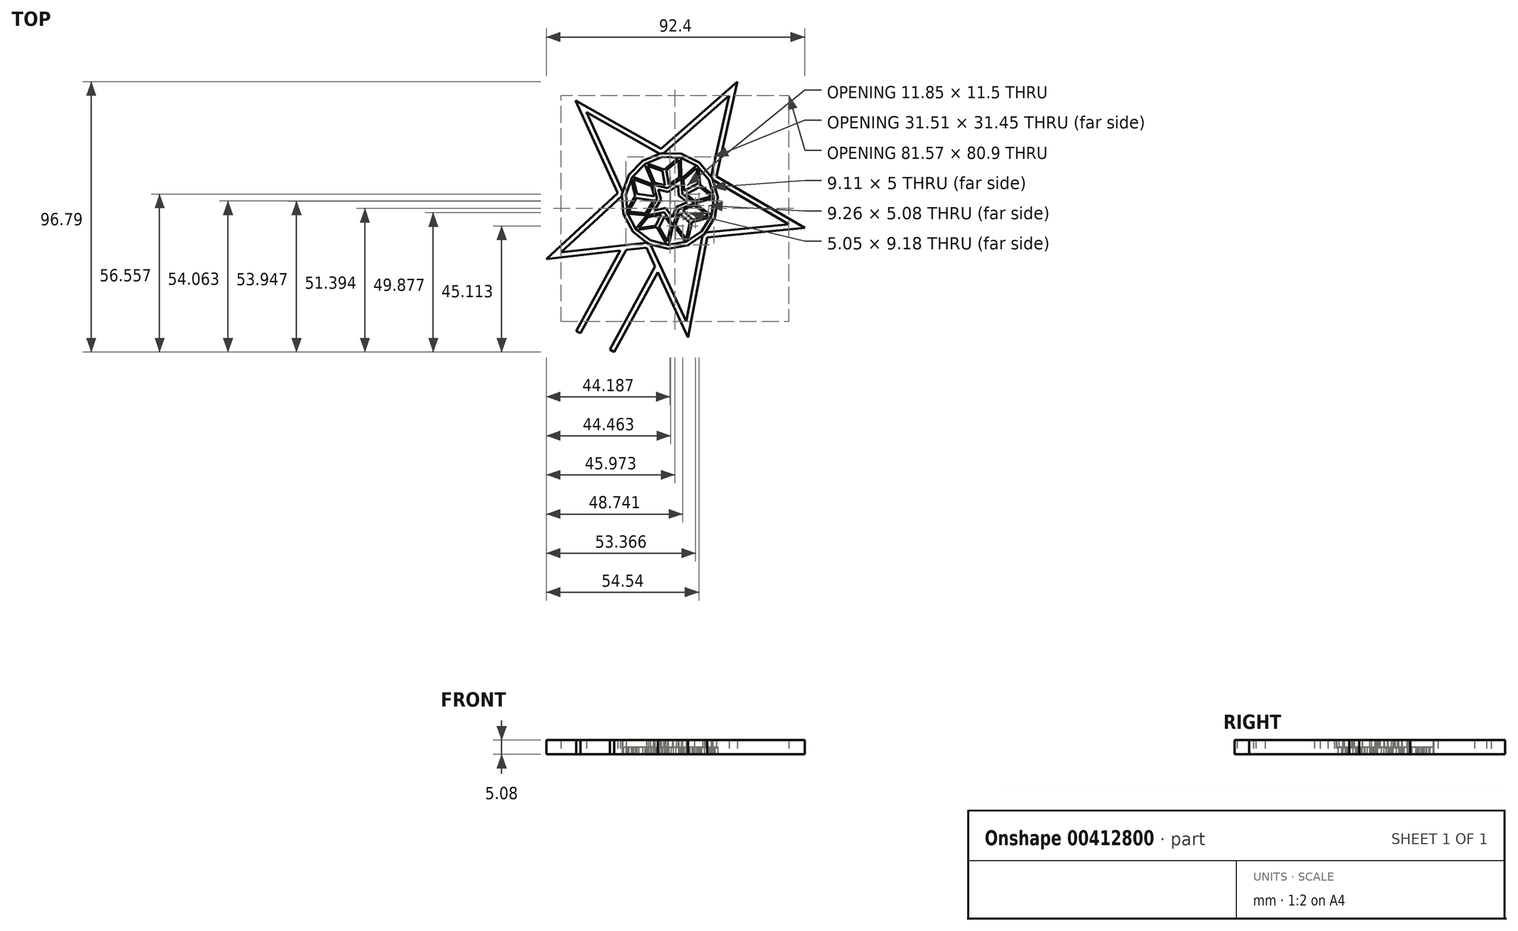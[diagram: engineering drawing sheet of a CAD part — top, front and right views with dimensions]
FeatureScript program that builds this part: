
annotation { "Feature Type Name" : "Feature", "Feature Type Description" : "" }
export const myFeature = defineFeature(function(context is Context, id is Id, definition is map)
    precondition{}
    {
        {
            var Q0;
            Q0=qCreatedBy(makeId("Top.planeOp"),FACE);
            var sketch = newSketch(context, id + "F0", { "sketchPlane" : qUnion([Q0])});
            skLineSegment(sketch, "E0", {"start": v(-1.96, 11.1) * mm, "end": v(-0.8, 4.49) * mm});
            skLineSegment(sketch, "E1", {"start": v(7.94, -7.66) * mm, "end": v(3.28, -3.16) * mm});
            skLineSegment(sketch, "E2", {"start": v(10.8, 5.75) * mm, "end": v(4.51, 2.4) * mm});
            skLineSegment(sketch, "E3", {"start": v(-12.4, 1.73) * mm, "end": v(-4.51, 0.63) * mm});
            skLineSegment(sketch, "E4", {"start": v(-4.65, -9.55) * mm, "end": v(-2, -4.1) * mm});
            skPoint(sketch, "E5.cCircle.perimeterSnap0", {"position": v(15.6, 4.49) * mm});
            skPoint(sketch, "E5.0.startSnap0", {"position": v(15.6, 4.49) * mm});
            skLineSegment(sketch, "E6", {"start": v(-8.26, 13.38) * mm, "end": v(-1.96, 11.1) * mm});
            skLineSegment(sketch, "E7", {"start": v(-1.96, 11.1) * mm, "end": v(3.16, 15.4) * mm});
            skLineSegment(sketch, "E8", {"start": v(10.8, 5.75) * mm, "end": v(10.32, 11.82) * mm});
            skLineSegment(sketch, "E9", {"start": v(10.8, 5.75) * mm, "end": v(15.57, 1.96) * mm});
            skLineSegment(sketch, "E10", {"start": v(6.46, -14.34) * mm, "end": v(7.94, -7.66) * mm});
            skLineSegment(sketch, "E11", {"start": v(7.94, -7.66) * mm, "end": v(14.57, -5.94) * mm});
            skLineSegment(sketch, "E12", {"start": v(-4.65, -9.55) * mm, "end": v(-1.08, -15.7) * mm});
            skLineSegment(sketch, "E13", {"start": v(-11.7, -10.54) * mm, "end": v(-4.65, -9.55) * mm});
            skLineSegment(sketch, "E14", {"start": v(-15.3, -3.42) * mm, "end": v(-12.4, 1.73) * mm});
            skLineSegment(sketch, "E15", {"start": v(-13.77, 7.5) * mm, "end": v(-12.4, 1.73) * mm});
            skLineSegment(sketch, "E16", {"start": v(-0.8, 4.49) * mm, "end": v(4.12, 7.8) * mm});
            skLineSegment(sketch, "E17", {"start": v(4.51, 2.4) * mm, "end": v(8.76, -0.93) * mm});
            skLineSegment(sketch, "E18", {"start": v(3.28, -3.16) * mm, "end": v(8.76, -0.93) * mm});
            skLineSegment(sketch, "E19", {"start": v(3.28, -3.16) * mm, "end": v(1.26, -8.69) * mm});
            skLineSegment(sketch, "E20", {"start": v(1.26, -8.69) * mm, "end": v(-2, -4.1) * mm});
            skLineSegment(sketch, "E21", {"start": v(-8.21, -5.33) * mm, "end": v(-2, -4.1) * mm});
            skLineSegment(sketch, "E22", {"start": v(-8.21, -5.33) * mm, "end": v(-4.51, 0.63) * mm});
            skLineSegment(sketch, "E23", {"start": v(-5.98, 5.76) * mm, "end": v(-4.51, 0.63) * mm});
            skLineSegment(sketch, "E24", {"start": v(-5.98, 5.76) * mm, "end": v(-0.8, 4.49) * mm});
            skLineSegment(sketch, "E25", {"start": v(-2.2, 16.96) * mm, "end": v(21.23, 37.66) * mm});
            skLineSegment(sketch, "E26", {"start": v(14.83, 8.59) * mm, "end": v(21.23, 37.66) * mm});
            skLineSegment(sketch, "E27", {"start": v(15.45, 7.34) * mm, "end": v(42.63, -8.47) * mm});
            skLineSegment(sketch, "E28", {"start": v(42.63, -8.47) * mm, "end": v(12.75, -11.45) * mm});
            skLineSegment(sketch, "E29", {"start": v(5.85, -43.24) * mm, "end": v(11.78, -12.4) * mm});
            skLineSegment(sketch, "E30", {"start": v(-6.93, -15.67) * mm, "end": v(5.85, -43.24) * mm});
            skLineSegment(sketch, "E31", {"start": v(-38.94, -18.5) * mm, "end": v(-8.17, -15.03) * mm});
            skLineSegment(sketch, "E32", {"start": v(-17.04, 1.75) * mm, "end": v(-38.94, -18.5) * mm});
            skLineSegment(sketch, "E33", {"start": v(-16.82, 3.13) * mm, "end": v(-29.8, 31.65) * mm});
            skLineSegment(sketch, "E34", {"start": v(-29.8, 31.65) * mm, "end": v(-3.6, 16.75) * mm});
            skPoint(sketch, "E35.orphan", {"position": v(-1.45, 8.17) * mm});
            skLineSegment(sketch, "E36", {"start": v(4.12, 7.8) * mm, "end": v(4.51, 2.4) * mm});
            skLineSegment(sketch, "E37", {"start": v(-13.33, 8.5) * mm, "end": v(-5.98, 5.76) * mm});
            skLineSegment(sketch, "E38", {"start": v(4.12, 7.8) * mm, "end": v(4.02, 15.29) * mm});
            skLineSegment(sketch, "E39", {"start": v(-8.99, 13.02) * mm, "end": v(-5.98, 5.76) * mm});
            skLineSegment(sketch, "E40", {"start": v(4.12, 7.8) * mm, "end": v(9.6, 12.56) * mm});
            skLineSegment(sketch, "E41", {"start": v(-8.21, -5.33) * mm, "end": v(-15.08, -4.67) * mm});
            skLineSegment(sketch, "E42", {"start": v(-8.21, -5.33) * mm, "end": v(-12.2, -10.07) * mm});
            skLineSegment(sketch, "E43", {"start": v(-0.39, -15.81) * mm, "end": v(1.26, -8.69) * mm});
            skLineSegment(sketch, "E44", {"start": v(5.74, -14.73) * mm, "end": v(1.26, -8.69) * mm});
            skLineSegment(sketch, "E45", {"start": v(8.76, -0.93) * mm, "end": v(15.79, 0.96) * mm});
            skLineSegment(sketch, "E46.0", {"start": v(-18.6, 2.73) * mm, "end": v(-44.13, -20.87) * mm});
            skLineSegment(sketch, "E46.1", {"start": v(-44.13, -20.87) * mm, "end": v(-8.34, -16.84) * mm});
            skLineSegment(sketch, "E46.2", {"start": v(-18.6, 2.73) * mm, "end": v(-33.7, 35.9) * mm});
            skLineSegment(sketch, "E46.3", {"start": v(-8.34, -16.84) * mm, "end": v(6.56, -48.99) * mm});
            skLineSegment(sketch, "E46.4", {"start": v(6.56, -48.99) * mm, "end": v(13.45, -13.16) * mm});
            skLineSegment(sketch, "E46.5", {"start": v(48.27, -9.7) * mm, "end": v(13.45, -13.16) * mm});
            skLineSegment(sketch, "E46.6", {"start": v(-33.7, 35.9) * mm, "end": v(-3.12, 18.52) * mm});
            skLineSegment(sketch, "E46.7", {"start": v(-3.12, 18.52) * mm, "end": v(24.14, 42.6) * mm});
            skLineSegment(sketch, "E46.8", {"start": v(16.67, 8.69) * mm, "end": v(24.14, 42.6) * mm});
            skLineSegment(sketch, "E46.9", {"start": v(16.67, 8.69) * mm, "end": v(48.27, -9.7) * mm});
            skLineSegment(sketch, "E47", {"start": v(8.76, -0.93) * mm, "end": v(14.93, -5.2) * mm});
            skLineSegment(sketch, "E48.0", {"start": v(-0.55, 3.12) * mm, "end": v(3.01, 5.52) * mm});
            skLineSegment(sketch, "E48.1", {"start": v(-4.15, 4) * mm, "end": v(-0.55, 3.12) * mm});
            skLineSegment(sketch, "E48.2", {"start": v(3.01, 5.52) * mm, "end": v(3.29, 1.75) * mm});
            skLineSegment(sketch, "E48.3", {"start": v(-4.15, 4) * mm, "end": v(-3.14, 0.44) * mm});
            skLineSegment(sketch, "E48.4", {"start": v(-5.6, -3.51) * mm, "end": v(-3.14, 0.44) * mm});
            skLineSegment(sketch, "E48.5", {"start": v(-5.6, -3.51) * mm, "end": v(-1.43, -2.7) * mm});
            skLineSegment(sketch, "E48.6", {"start": v(3.29, 1.75) * mm, "end": v(6.26, -0.58) * mm});
            skLineSegment(sketch, "E48.7", {"start": v(2.28, -2.2) * mm, "end": v(6.26, -0.58) * mm});
            skLineSegment(sketch, "E48.8", {"start": v(2.28, -2.2) * mm, "end": v(0.9, -5.98) * mm});
            skLineSegment(sketch, "E48.9", {"start": v(0.9, -5.98) * mm, "end": v(-1.43, -2.7) * mm});
            skLineSegment(sketch, "E49.0", {"start": v(-17.09, 2.4) * mm, "end": v(-14.64, 9.13) * mm});
            skLineSegment(sketch, "E49.1", {"start": v(-16.58, -4.77) * mm, "end": v(-17.09, 2.4) * mm});
            skLineSegment(sketch, "E49.2", {"start": v(-13.2, -11.1) * mm, "end": v(-16.58, -4.77) * mm});
            skLineSegment(sketch, "E49.3", {"start": v(-7.55, -15.51) * mm, "end": v(-13.2, -11.1) * mm});
            skLineSegment(sketch, "E49.4", {"start": v(10.61, 13.6) * mm, "end": v(15.23, 8.1) * mm});
            skLineSegment(sketch, "E49.5", {"start": v(4.16, 16.74) * mm, "end": v(10.61, 13.6) * mm});
            skLineSegment(sketch, "E49.6", {"start": v(-3, 16.99) * mm, "end": v(4.16, 16.74) * mm});
            skLineSegment(sketch, "E49.7", {"start": v(-9.66, 14.3) * mm, "end": v(-3, 16.99) * mm});
            skLineSegment(sketch, "E49.8", {"start": v(15.23, 8.1) * mm, "end": v(17.2, 1.21) * mm});
            skLineSegment(sketch, "E49.9", {"start": v(17.2, 1.21) * mm, "end": v(16.22, -5.9) * mm});
            skLineSegment(sketch, "E49.10", {"start": v(16.22, -5.9) * mm, "end": v(12.42, -11.98) * mm});
            skLineSegment(sketch, "E49.11", {"start": v(12.42, -11.98) * mm, "end": v(6.47, -16) * mm});
            skLineSegment(sketch, "E49.12", {"start": v(-14.64, 9.13) * mm, "end": v(-9.66, 14.3) * mm});
            skLineSegment(sketch, "E49.13", {"start": v(6.47, -16) * mm, "end": v(-0.6, -17.24) * mm});
            skLineSegment(sketch, "E49.14", {"start": v(-0.6, -17.24) * mm, "end": v(-7.55, -15.51) * mm});
            skLineSegment(sketch, "E50.0", {"start": v(-12, 0.93) * mm, "end": v(-5.74, 0.06) * mm});
            skLineSegment(sketch, "E50.1", {"start": v(-14.76, -3.96) * mm, "end": v(-12, 0.93) * mm});
            skLineSegment(sketch, "E50.2", {"start": v(-8.6, -4.55) * mm, "end": v(-14.76, -3.96) * mm});
            skLineSegment(sketch, "E50.3", {"start": v(-8.6, -4.55) * mm, "end": v(-5.74, 0.06) * mm});
            skLineSegment(sketch, "E51.0", {"start": v(-13.05, 7.62) * mm, "end": v(-6.58, 5.2) * mm});
            skLineSegment(sketch, "E51.1", {"start": v(-13.05, 7.62) * mm, "end": v(-11.8, 2.4) * mm});
            skLineSegment(sketch, "E51.2", {"start": v(-11.8, 2.4) * mm, "end": v(-5.53, 1.52) * mm});
            skLineSegment(sketch, "E51.3", {"start": v(-6.58, 5.2) * mm, "end": v(-5.53, 1.52) * mm});
            skLineSegment(sketch, "E52.0", {"start": v(-7.97, 12.5) * mm, "end": v(-2.62, 10.55) * mm});
            skLineSegment(sketch, "E52.1", {"start": v(-7.97, 12.5) * mm, "end": v(-5.44, 6.39) * mm});
            skLineSegment(sketch, "E52.2", {"start": v(-5.44, 6.39) * mm, "end": v(-1.72, 5.47) * mm});
            skLineSegment(sketch, "E52.3", {"start": v(-2.62, 10.55) * mm, "end": v(-1.72, 5.47) * mm});
            skLineSegment(sketch, "E53.0", {"start": v(-1.17, 10.8) * mm, "end": v(3.3, 14.55) * mm});
            skLineSegment(sketch, "E53.1", {"start": v(-1.17, 10.8) * mm, "end": v(-0.27, 5.73) * mm});
            skLineSegment(sketch, "E53.2", {"start": v(-0.27, 5.73) * mm, "end": v(3.38, 8.18) * mm});
            skLineSegment(sketch, "E53.3", {"start": v(3.38, 8.18) * mm, "end": v(3.3, 14.55) * mm});
            skLineSegment(sketch, "E54.0", {"start": v(4.88, 7.48) * mm, "end": v(9.6, 11.58) * mm});
            skLineSegment(sketch, "E54.1", {"start": v(4.88, 7.48) * mm, "end": v(5.16, 3.58) * mm});
            skLineSegment(sketch, "E54.2", {"start": v(10.03, 6.18) * mm, "end": v(5.16, 3.58) * mm});
            skLineSegment(sketch, "E54.3", {"start": v(10.03, 6.18) * mm, "end": v(9.6, 11.58) * mm});
            skLineSegment(sketch, "E55.0", {"start": v(10.72, 4.88) * mm, "end": v(14.96, 1.5) * mm});
            skLineSegment(sketch, "E55.1", {"start": v(10.72, 4.88) * mm, "end": v(5.86, 2.28) * mm});
            skLineSegment(sketch, "E55.2", {"start": v(5.86, 2.28) * mm, "end": v(8.93, -0.12) * mm});
            skLineSegment(sketch, "E55.3", {"start": v(8.93, -0.12) * mm, "end": v(14.96, 1.5) * mm});
            skLineSegment(sketch, "E56.0", {"start": v(4.6, -3.42) * mm, "end": v(8.67, -1.76) * mm});
            skLineSegment(sketch, "E56.1", {"start": v(8.16, -6.84) * mm, "end": v(4.6, -3.42) * mm});
            skLineSegment(sketch, "E56.2", {"start": v(8.16, -6.84) * mm, "end": v(13.87, -5.36) * mm});
            skLineSegment(sketch, "E56.3", {"start": v(8.67, -1.76) * mm, "end": v(13.87, -5.36) * mm});
            skLineSegment(sketch, "E57.0", {"start": v(3.58, -4.48) * mm, "end": v(2.09, -8.57) * mm});
            skLineSegment(sketch, "E57.1", {"start": v(7.13, -7.9) * mm, "end": v(3.58, -4.48) * mm});
            skLineSegment(sketch, "E57.2", {"start": v(5.86, -13.65) * mm, "end": v(7.13, -7.9) * mm});
            skLineSegment(sketch, "E57.3", {"start": v(5.86, -13.65) * mm, "end": v(2.09, -8.57) * mm});
            skLineSegment(sketch, "E58.0", {"start": v(-3.81, -9.52) * mm, "end": v(-1.88, -5.54) * mm});
            skLineSegment(sketch, "E58.1", {"start": v(-3.81, -9.52) * mm, "end": v(-0.87, -14.6) * mm});
            skLineSegment(sketch, "E58.2", {"start": v(-0.87, -14.6) * mm, "end": v(0.47, -8.84) * mm});
            skLineSegment(sketch, "E58.3", {"start": v(0.47, -8.84) * mm, "end": v(-1.88, -5.54) * mm});
            skLineSegment(sketch, "E59.0", {"start": v(-7.87, -5.9) * mm, "end": v(-3.12, -4.97) * mm});
            skLineSegment(sketch, "E59.1", {"start": v(-7.87, -5.9) * mm, "end": v(-11.16, -9.82) * mm});
            skLineSegment(sketch, "E59.2", {"start": v(-11.16, -9.82) * mm, "end": v(-5.07, -8.96) * mm});
            skLineSegment(sketch, "E59.3", {"start": v(-5.07, -8.96) * mm, "end": v(-3.12, -4.97) * mm});
            skLineSegment(sketch, "E60.0", {"start": v(-15.7, 2.2) * mm, "end": v(-13.45, 8.4) * mm});
            skLineSegment(sketch, "E60.1", {"start": v(-15.23, -4.38) * mm, "end": v(-15.7, 2.2) * mm});
            skLineSegment(sketch, "E60.2", {"start": v(-12.14, -10.2) * mm, "end": v(-15.23, -4.38) * mm});
            skLineSegment(sketch, "E60.3", {"start": v(-6.94, -14.25) * mm, "end": v(-12.14, -10.2) * mm});
            skLineSegment(sketch, "E60.4", {"start": v(9.75, 12.5) * mm, "end": v(14, 7.45) * mm});
            skLineSegment(sketch, "E60.5", {"start": v(3.82, 15.38) * mm, "end": v(9.75, 12.5) * mm});
            skLineSegment(sketch, "E60.6", {"start": v(-2.76, 15.6) * mm, "end": v(3.82, 15.38) * mm});
            skLineSegment(sketch, "E60.7", {"start": v(-8.87, 13.13) * mm, "end": v(-2.76, 15.6) * mm});
            skLineSegment(sketch, "E60.8", {"start": v(14, 7.45) * mm, "end": v(15.81, 1.12) * mm});
            skLineSegment(sketch, "E60.9", {"start": v(15.81, 1.12) * mm, "end": v(14.9, -5.41) * mm});
            skLineSegment(sketch, "E60.10", {"start": v(14.9, -5.41) * mm, "end": v(11.4, -11) * mm});
            skLineSegment(sketch, "E60.11", {"start": v(11.4, -11) * mm, "end": v(5.95, -14.7) * mm});
            skLineSegment(sketch, "E60.12", {"start": v(-13.45, 8.4) * mm, "end": v(-8.87, 13.13) * mm});
            skLineSegment(sketch, "E60.13", {"start": v(5.95, -14.7) * mm, "end": v(-0.54, -15.84) * mm});
            skLineSegment(sketch, "E60.14", {"start": v(-0.54, -15.84) * mm, "end": v(-6.94, -14.25) * mm});
            skPoint(sketch, "E61.orphan", {"position": v(16.56, 1.17) * mm});
            skPoint(sketch, "E62.0.start.orphan", {"position": v(-2.9, 16.35) * mm});
            skPoint(sketch, "E62.2.end.orphan", {"position": v(14.65, 7.8) * mm});
            skPoint(sketch, "E62.cCircle.center.orphan", {"position": v(0, 0) * mm});
            skLineSegment(sketch, "E63", {"start": v(-51.26, -46.77) * mm, "end": v(-51.34, -46.87) * mm});
            skPoint(sketch, "E64.start.orphan", {"position": v(0, -34.84) * mm});
            skLineSegment(sketch, "E65", {"start": v(-15.6, -17.66) * mm, "end": v(-31.92, -47.51) * mm});
            skLineSegment(sketch, "E66.MirrorCS", {"start": v(-5.1, -23.4) * mm, "end": v(-21.46, -53.32) * mm});
            skLineSegment(sketch, "E67.0", {"start": v(-17.77, -17.9) * mm, "end": v(-33.48, -46.65) * mm});
            skLineSegment(sketch, "E68.0", {"start": v(-4.28, -25.6) * mm, "end": v(-19.9, -54.18) * mm});
            skLineSegment(sketch, "E69", {"start": v(-33.48, -46.65) * mm, "end": v(-31.92, -47.51) * mm});
            skLineSegment(sketch, "E70.trimOffspring", {"start": v(-21.46, -53.32) * mm, "end": v(-19.9, -54.18) * mm});
            skPoint(sketch, "E71.orphan", {"position": v(-48.1, -77.1) * mm});
            skPoint(sketch, "E72.orphan", {"position": v(-37.6, -82.84) * mm});
            skLineSegment(sketch, "E73.trimOffspring", {"start": v(5, 7.58) * mm, "end": v(4.89, 7.38) * mm});
            skSolve(sketch);
        }
        {
            var Q0;
            {var subQ44=sQuery(id+"F0.wireOp",EDGE,"E49.2");Q0=makeQuery(id+"F0.imprint","IMPRINT",FACE,{"disambiguationData":[TD([[makeQuery(id+"F0.imprint","IMPRINT",EDGE,{"derivedFrom":subQ44}),-1.0]])]});}
            extrude(context, id + "F1", {"entities" : qUnion([Q0]), "depth" : 2.54 * mm});
        }
        {
            var Q0;
            {var subQ20=sQuery(id+"F0.wireOp",EDGE,"E25");Q0=makeQuery(id+"F0.imprint","IMPRINT",FACE,{"disambiguationData":[TD([[makeQuery(id+"F0.imprint","IMPRINT",EDGE,{"derivedFrom":subQ20}),1.0]])]});}
            var Q1;
            {var subQ0=sQuery(id+"F0.wireOp",EDGE,"E65");Q1=makeQuery(id+"F0.imprint","IMPRINT",FACE,{"disambiguationData":[TD([[makeQuery(id+"F0.imprint","IMPRINT",EDGE,{"derivedFrom":subQ0}),-1.0]])]});}
            var Q2;
            {var subQ0=sQuery(id+"F0.wireOp",EDGE,"E68.0");Q2=makeQuery(id+"F0.imprint","IMPRINT",FACE,{"disambiguationData":[TD([[makeQuery(id+"F0.imprint","IMPRINT",EDGE,{"derivedFrom":subQ0}),-1.0]])]});}
            var Q3;
            Q3=makeQuery(id+"F0.imprint","IMPRINT",FACE,{"disambiguationData":[TD([[makeQuery(id+"F0.imprint","IMPRINT",EDGE,{"derivedFrom":sQuery(id+"F0.wireOp",EDGE,"E16")}),-1.0]])]});
            extrude(context, id + "F2", {"entities" : qUnion([Q0, Q1, Q2, Q3]), "depth" : 5.08 * mm});
        }
        {
            var Q0;
            Q0=makeQuery(id+"F0.imprint","IMPRINT",FACE,{"disambiguationData":[TD([[makeQuery(id+"F0.imprint","IMPRINT",EDGE,{"derivedFrom":sQuery(id+"F0.wireOp",EDGE,"E3")}),1.0]])]});
            var Q1;
            Q1=makeQuery(id+"F0.imprint","IMPRINT",FACE,{"disambiguationData":[TD([[makeQuery(id+"F0.imprint","IMPRINT",EDGE,{"derivedFrom":sQuery(id+"F0.wireOp",EDGE,"E3")}),-1.0]])]});
            var Q2;
            Q2=makeQuery(id+"F0.imprint","IMPRINT",FACE,{"disambiguationData":[TD([[makeQuery(id+"F0.imprint","IMPRINT",EDGE,{"derivedFrom":sQuery(id+"F0.wireOp",EDGE,"E0")}),-1.0]])]});
            var Q3;
            Q3=makeQuery(id+"F0.imprint","IMPRINT",FACE,{"disambiguationData":[TD([[makeQuery(id+"F0.imprint","IMPRINT",EDGE,{"derivedFrom":sQuery(id+"F0.wireOp",EDGE,"E0")}),1.0]])]});
            var Q4;
            Q4=makeQuery(id+"F0.imprint","IMPRINT",FACE,{"disambiguationData":[TD([[makeQuery(id+"F0.imprint","IMPRINT",EDGE,{"derivedFrom":sQuery(id+"F0.wireOp",EDGE,"E2")}),-1.0]])]});
            var Q5;
            Q5=makeQuery(id+"F0.imprint","IMPRINT",FACE,{"disambiguationData":[TD([[makeQuery(id+"F0.imprint","IMPRINT",EDGE,{"derivedFrom":sQuery(id+"F0.wireOp",EDGE,"E2")}),1.0]])]});
            var Q6;
            Q6=makeQuery(id+"F0.imprint","IMPRINT",FACE,{"disambiguationData":[TD([[makeQuery(id+"F0.imprint","IMPRINT",EDGE,{"derivedFrom":sQuery(id+"F0.wireOp",EDGE,"E1")}),-1.0]])]});
            var Q7;
            Q7=makeQuery(id+"F0.imprint","IMPRINT",FACE,{"disambiguationData":[TD([[makeQuery(id+"F0.imprint","IMPRINT",EDGE,{"derivedFrom":sQuery(id+"F0.wireOp",EDGE,"E1")}),1.0]])]});
            var Q8;
            Q8=makeQuery(id+"F0.imprint","IMPRINT",FACE,{"disambiguationData":[TD([[makeQuery(id+"F0.imprint","IMPRINT",EDGE,{"derivedFrom":sQuery(id+"F0.wireOp",EDGE,"E4")}),-1.0]])]});
            var Q9;
            Q9=makeQuery(id+"F0.imprint","IMPRINT",FACE,{"disambiguationData":[TD([[makeQuery(id+"F0.imprint","IMPRINT",EDGE,{"derivedFrom":sQuery(id+"F0.wireOp",EDGE,"E4")}),1.0]])]});
            extrude(context, id + "F3", {"entities" : qUnion([Q0, Q1, Q2, Q3, Q4, Q5, Q6, Q7, Q8, Q9]), "depth" : 2.54 * mm});
        }
    });
